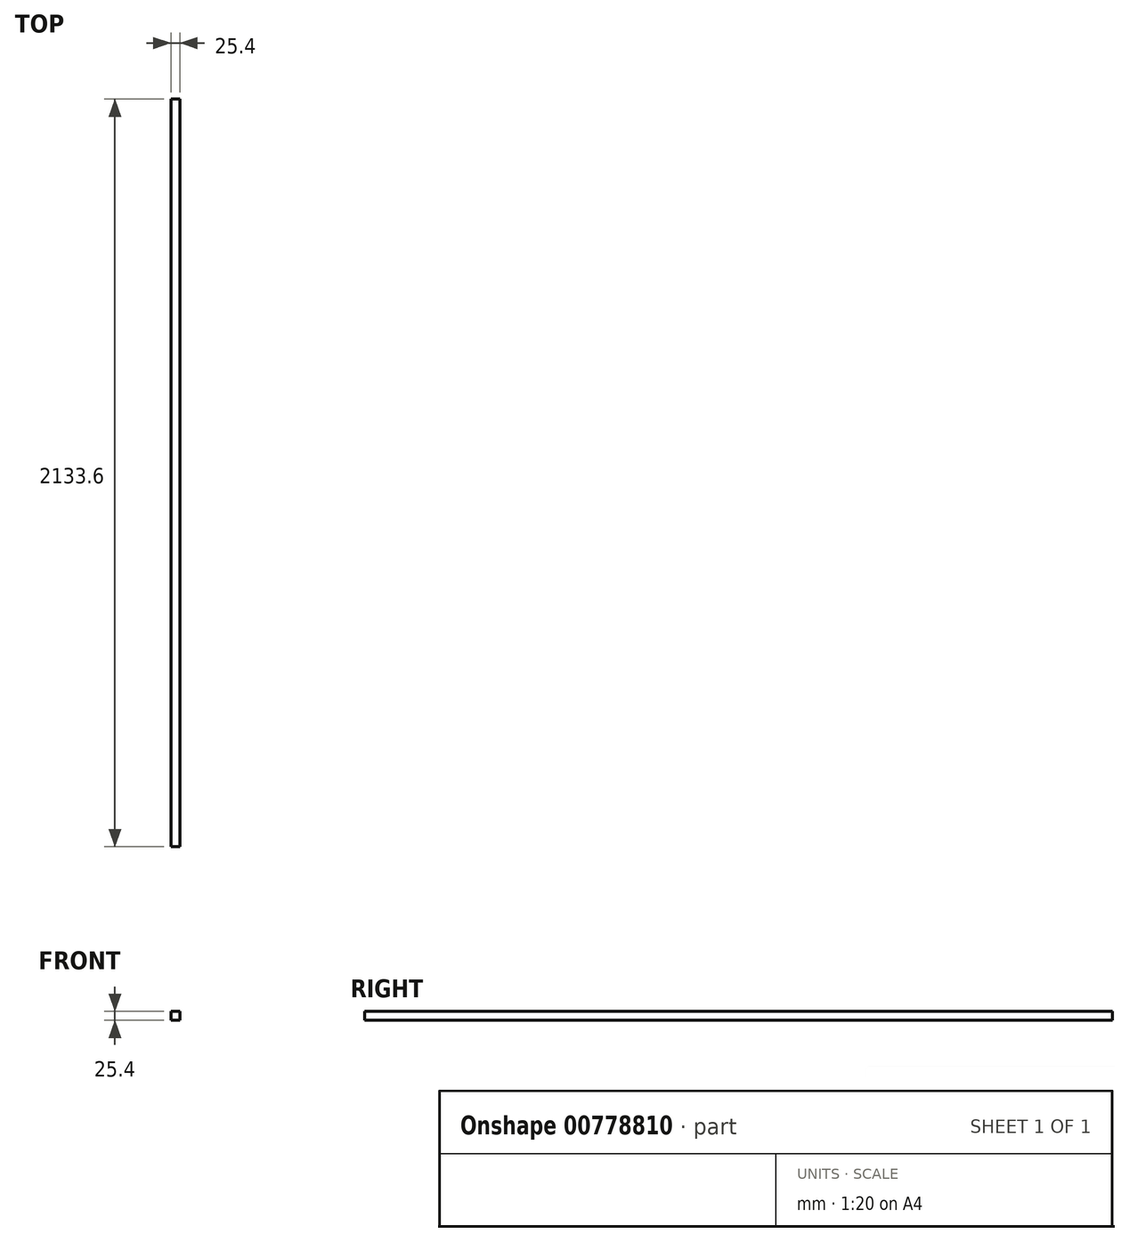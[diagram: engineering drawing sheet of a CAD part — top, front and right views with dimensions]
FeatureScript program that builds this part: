
annotation { "Feature Type Name" : "Feature", "Feature Type Description" : "" }
export const myFeature = defineFeature(function(context is Context, id is Id, definition is map)
    precondition{}
    {
        {
            var Q0;
            Q0=qCreatedBy(makeId("Front.planeOp"),FACE);
            var sketch = newSketch(context, id + "F0", { "sketchPlane" : qUnion([Q0])});
            skLineSegment(sketch, "E0.bottom", {"start": v(0, 0) * mm, "end": v(25.4, 0) * mm});
            skLineSegment(sketch, "E0.top", {"start": v(0, 25.4) * mm, "end": v(25.4, 25.4) * mm});
            skLineSegment(sketch, "E0.left", {"start": v(0, 0) * mm, "end": v(0, 25.4) * mm});
            skLineSegment(sketch, "E0.right", {"start": v(25.4, 0) * mm, "end": v(25.4, 25.4) * mm});
            skSolve(sketch);
        }
        {
            var Q0;
            Q0=makeQuery(id+"F0.imprint","IMPRINT",FACE,{"disambiguationData":[TD([[makeQuery(id+"F0.imprint","IMPRINT",EDGE,{"derivedFrom":sQuery(id+"F0.wireOp",EDGE,"E0.bottom")}),1.0]])]});
            extrude(context, id + "F1", {"entities" : qUnion([Q0]), "depth" : 2133.6 * mm, "offsetDistance" : 25.4 * mm});
        }
    });
